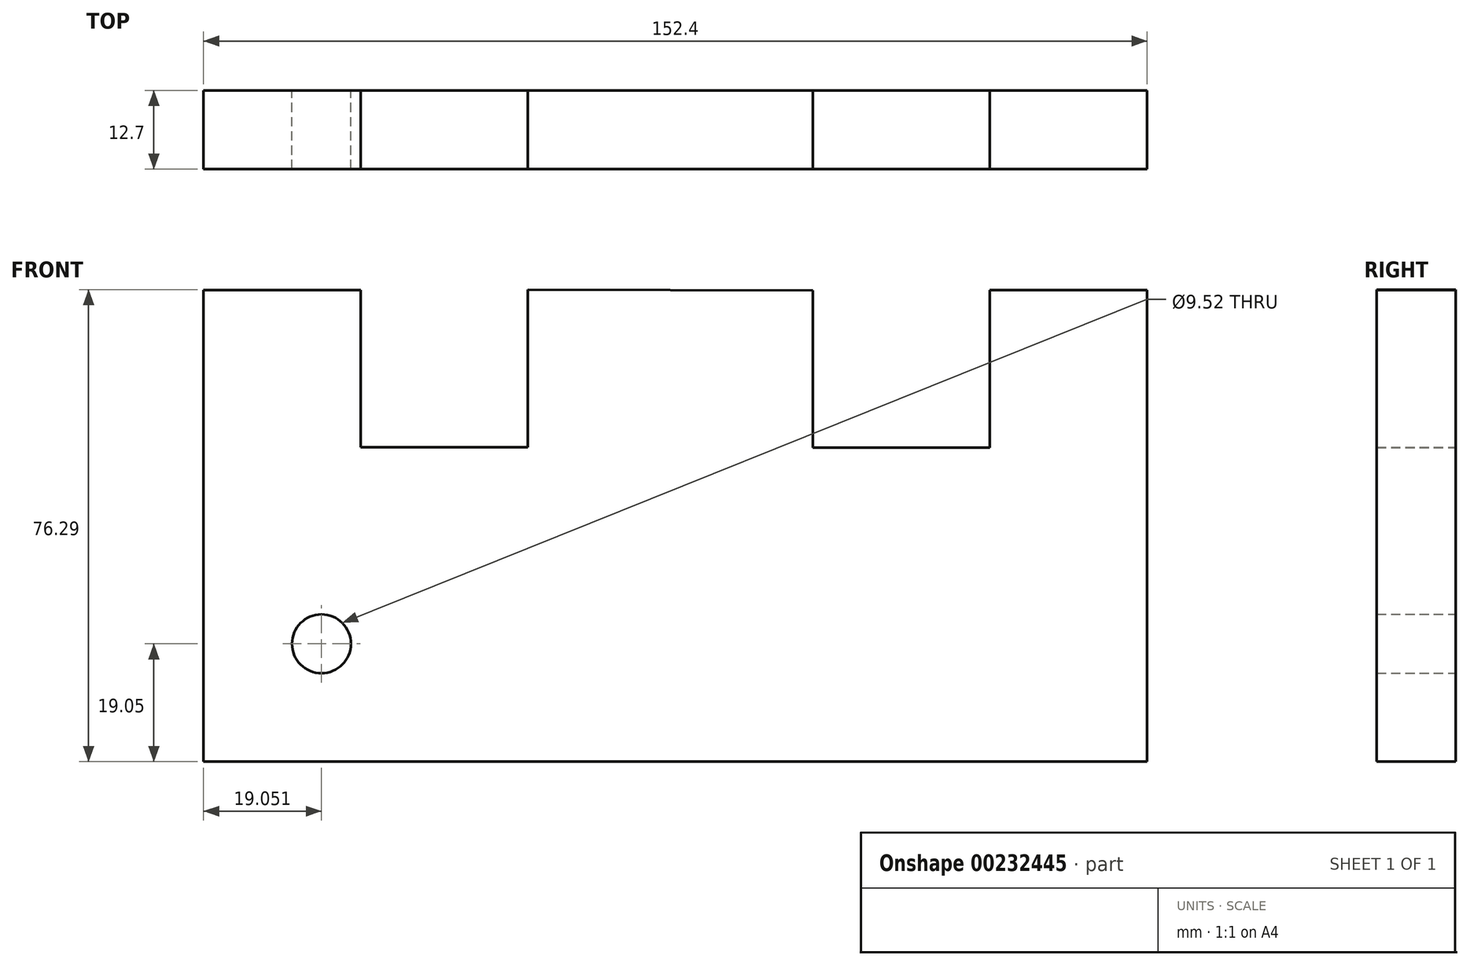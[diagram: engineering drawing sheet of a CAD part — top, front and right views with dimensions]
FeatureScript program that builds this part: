
annotation { "Feature Type Name" : "Feature", "Feature Type Description" : "" }
export const myFeature = defineFeature(function(context is Context, id is Id, definition is map)
    precondition{}
    {
        {
            var Q0;
            Q0=qCreatedBy(makeId("Front.planeOp"),FACE);
            var sketch = newSketch(context, id + "F0", { "sketchPlane" : qUnion([Q0])});
            skLineSegment(sketch, "E0", {"start": v(-73.7, 57.15) * mm, "end": v(-73.7, -19.05) * mm});
            skLineSegment(sketch, "E1", {"start": v(-73.7, -19.05) * mm, "end": v(78.7, -19.05) * mm});
            skLineSegment(sketch, "E2", {"start": v(78.7, -19.05) * mm, "end": v(78.7, 57.15) * mm});
            skLineSegment(sketch, "E3", {"start": v(78.7, 57.15) * mm, "end": v(53.3, 57.15) * mm});
            skLineSegment(sketch, "E4", {"start": v(53.3, 57.15) * mm, "end": v(53.3, 31.73) * mm});
            skLineSegment(sketch, "E5", {"start": v(53.3, 31.73) * mm, "end": v(24.73, 31.73) * mm});
            skLineSegment(sketch, "E6", {"start": v(24.73, 31.73) * mm, "end": v(24.73, 57.13) * mm});
            skLineSegment(sketch, "E7", {"start": v(-73.7, 57.15) * mm, "end": v(-48.3, 57.15) * mm});
            skLineSegment(sketch, "E8", {"start": v(-48.3, 57.15) * mm, "end": v(-48.3, 31.75) * mm});
            skLineSegment(sketch, "E9", {"start": v(-48.3, 31.75) * mm, "end": v(-21.31, 31.75) * mm});
            skLineSegment(sketch, "E10", {"start": v(-21.31, 31.75) * mm, "end": v(-21.31, 57.24) * mm});
            skLineSegment(sketch, "E11", {"start": v(-21.31, 57.24) * mm, "end": v(24.73, 57.13) * mm});
            skCircle(sketch, "E12", {"center": v(-54.65, 0) * mm, "radius": 4.76 * mm});
            skSolve(sketch);
        }
        {
            var Q0;
            Q0 = qSketchRegion(id + "F0", true);
            extrude(context, id + "F1", {"entities" : qUnion([Q0]), "depth" : 12.7 * mm});
        }
    });
